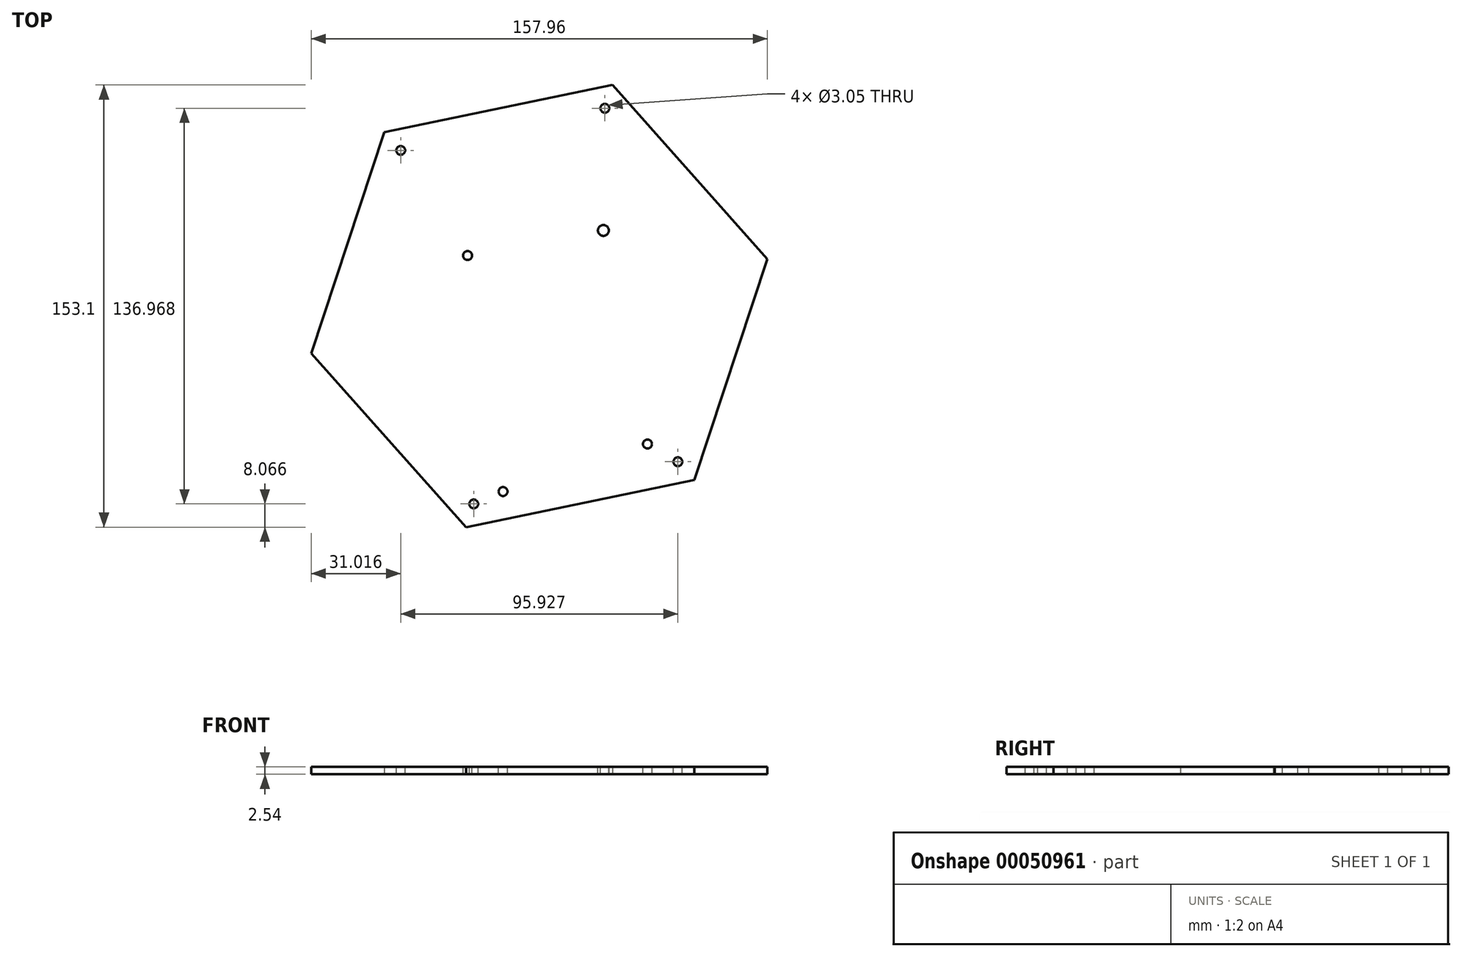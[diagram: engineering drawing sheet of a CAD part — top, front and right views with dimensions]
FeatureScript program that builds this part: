
annotation { "Feature Type Name" : "Feature", "Feature Type Description" : "" }
export const myFeature = defineFeature(function(context is Context, id is Id, definition is map)
    precondition{}
    {
        {
            var Q0;
            Q0=qCreatedBy(makeId("Top.planeOp"),FACE);
            var sketch = newSketch(context, id + "F0", { "sketchPlane" : qUnion([Q0])});
            skCircle(sketch, "E0.cCircle", {"center": v(0, 0) * mm, "radius": 69.84 * mm, "construction": true});
            skLineSegment(sketch, "E0.0", {"start": v(-53.61, 60.24) * mm, "end": v(25.36, 76.55) * mm});
            skLineSegment(sketch, "E0.1", {"start": v(25.36, 76.55) * mm, "end": v(78.98, 16.31) * mm});
            skLineSegment(sketch, "E0.2", {"start": v(78.98, 16.31) * mm, "end": v(53.61, -60.24) * mm});
            skLineSegment(sketch, "E0.3", {"start": v(53.61, -60.24) * mm, "end": v(-25.36, -76.55) * mm});
            skLineSegment(sketch, "E0.4", {"start": v(-25.36, -76.55) * mm, "end": v(-78.98, -16.31) * mm});
            skLineSegment(sketch, "E0.5", {"start": v(-78.98, -16.31) * mm, "end": v(-53.61, 60.24) * mm});
            skPoint(sketch, "E0.0.midPoint", {"position": v(-14.13, 68.4) * mm});
            skSolve(sketch);
        }
        {
            var Q0;
            Q0=makeQuery(id+"F0.imprint","IMPRINT",FACE,{"disambiguationData":[TD([[makeQuery(id+"F0.imprint","IMPRINT",EDGE,{"derivedFrom":sQuery(id+"F0.wireOp",EDGE,"E0.0")}),-1.0]])]});
            extrude(context, id + "F1", {"entities" : qUnion([Q0]), "depth" : 2.54 * mm});
        }
        {
            var Q0;
            Q0=makeQuery(id+"F1.opExtrude","CAP_FACE",FACE,{"disambiguationData":[OSD([sQuery(id+"F0.wireOp",EDGE,"E0.0"),sQuery(id+"F0.wireOp",EDGE,"E0.1"),sQuery(id+"F0.wireOp",EDGE,"E0.2"),sQuery(id+"F0.wireOp",EDGE,"E0.3"),sQuery(id+"F0.wireOp",EDGE,"E0.4"),sQuery(id+"F0.wireOp",EDGE,"E0.5")])],"isStart":false});
            var sketch = newSketch(context, id + "F2", { "sketchPlane" : qUnion([Q0])});
            skLineSegment(sketch, "E1", {"start": v(-25.36, -76.55) * mm, "end": v(-22.7, -68.48) * mm});
            skLineSegment(sketch, "E2", {"start": v(53.61, -60.24) * mm, "end": v(47.96, -53.9) * mm});
            skLineSegment(sketch, "E3", {"start": v(25.36, 76.55) * mm, "end": v(22.7, 68.48) * mm});
            skLineSegment(sketch, "E4", {"start": v(-53.61, 60.24) * mm, "end": v(-47.96, 53.9) * mm});
            skCircle(sketch, "E5", {"center": v(-47.96, 53.9) * mm, "radius": 1.52 * mm});
            skCircle(sketch, "E6", {"center": v(22.7, 68.48) * mm, "radius": 1.52 * mm});
            skCircle(sketch, "E7", {"center": v(-22.7, -68.48) * mm, "radius": 1.52 * mm});
            skCircle(sketch, "E8", {"center": v(47.96, -53.9) * mm, "radius": 1.52 * mm});
            skSolve(sketch);
        }
        {
            var Q0;
            Q0=makeQuery(id+"F2.imprint","IMPRINT",FACE,{"disambiguationData":[TD([[makeQuery(id+"F2.imprint","IMPRINT",EDGE,{"derivedFrom":sQuery(id+"F2.wireOp",EDGE,"E6")}),1.0]])]});
            var Q1;
            Q1=makeQuery(id+"F2.imprint","IMPRINT",FACE,{"disambiguationData":[TD([[makeQuery(id+"F2.imprint","IMPRINT",EDGE,{"derivedFrom":sQuery(id+"F2.wireOp",EDGE,"E5")}),1.0]])]});
            var Q2;
            Q2=makeQuery(id+"F2.imprint","IMPRINT",FACE,{"disambiguationData":[TD([[makeQuery(id+"F2.imprint","IMPRINT",EDGE,{"derivedFrom":sQuery(id+"F2.wireOp",EDGE,"E7")}),1.0]])]});
            var Q3;
            Q3=makeQuery(id+"F2.imprint","IMPRINT",FACE,{"disambiguationData":[TD([[makeQuery(id+"F2.imprint","IMPRINT",EDGE,{"derivedFrom":sQuery(id+"F2.wireOp",EDGE,"E8")}),1.0]])]});
            extrude(context, id + "F3", {"entities" : qUnion([Q0, Q1, Q2, Q3]), "operationType" : NewBodyOperationType.REMOVE, "oppositeDirection" : true, "depth" : 25.4 * mm});
        }
        {
            var Q0;
            Q0=makeQuery(id+"F1.opExtrude","CAP_FACE",FACE,{"disambiguationData":[OSD([sQuery(id+"F0.wireOp",EDGE,"E0.0"),sQuery(id+"F0.wireOp",EDGE,"E0.1"),sQuery(id+"F0.wireOp",EDGE,"E0.2"),sQuery(id+"F0.wireOp",EDGE,"E0.3"),sQuery(id+"F0.wireOp",EDGE,"E0.4"),sQuery(id+"F0.wireOp",EDGE,"E0.5")])],"isStart":false});
            var sketch = newSketch(context, id + "F4", { "sketchPlane" : qUnion([Q0])});
            skCircle(sketch, "E9", {"center": v(37.45, -47.75) * mm, "radius": 1.55 * mm});
            skCircle(sketch, "E10", {"center": v(-12.55, -64.2) * mm, "radius": 1.55 * mm});
            skCircle(sketch, "E11", {"center": v(22.18, 26.19) * mm, "radius": 1.88 * mm});
            skCircle(sketch, "E12", {"center": v(-24.82, 17.5) * mm, "radius": 1.55 * mm});
            skSolve(sketch);
        }
        {
            var Q0;
            Q0 = qSketchRegion(id + "F4", true);
            extrude(context, id + "F5", {"entities" : qUnion([Q0]), "operationType" : NewBodyOperationType.REMOVE, "oppositeDirection" : true, "depth" : 25.4 * mm});
        }
    });
